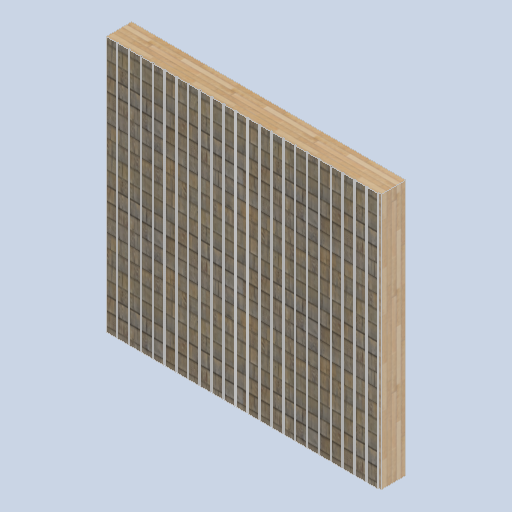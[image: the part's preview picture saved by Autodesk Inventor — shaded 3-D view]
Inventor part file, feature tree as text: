
AUTODESK INVENTOR PART (.ipt)
format: ipt  version: 2024.2 (Build 282272000, 272)  size: 416,768 bytes
history: native  units: in
note: dims shown in document units (in); Inventor stores cm internally (conversion verified against a paired STEP export)
features: other x3, sketch x1
ambient origin geometry x8: Origin, YZ Plane, XZ Plane, XY Plane, X Axis, Y Axis, Z Axis, Center Point
bodies: Solid1 (feature_tree)
feature tree (4):
  other  "front_wall_block05_MIR.ipt"
  other  "Solid1::front_wall_block05_MIR.ipt"
  other  "TaggingFeature1"
  sketch  "Sketch3"  dims[d0=0.3937in]
